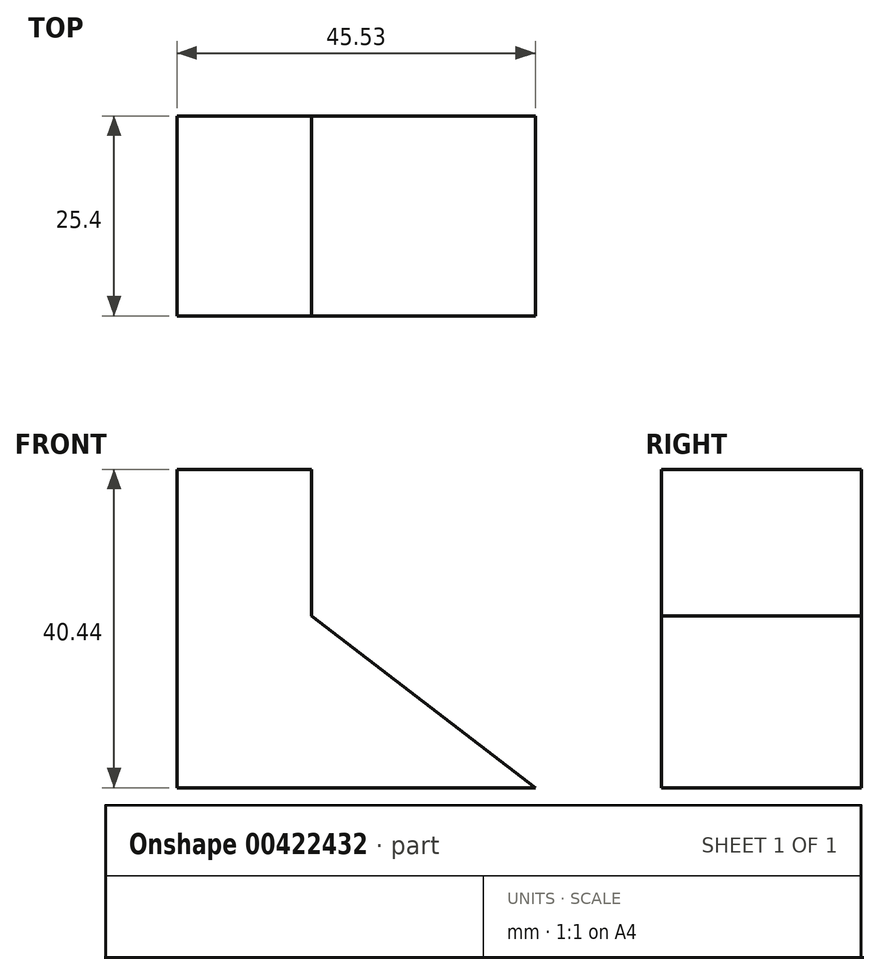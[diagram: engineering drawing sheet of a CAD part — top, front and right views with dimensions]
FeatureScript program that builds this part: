
annotation { "Feature Type Name" : "Feature", "Feature Type Description" : "" }
export const myFeature = defineFeature(function(context is Context, id is Id, definition is map)
    precondition{}
    {
        {
            var Q0;
            Q0=qCreatedBy(makeId("Front.planeOp"),FACE);
            var sketch = newSketch(context, id + "F0", { "sketchPlane" : qUnion([Q0])});
            skLineSegment(sketch, "E0", {"start": v(0, 0) * mm, "end": v(0, 40.44) * mm});
            skLineSegment(sketch, "E1", {"start": v(0, 40.44) * mm, "end": v(17.1, 40.44) * mm});
            skLineSegment(sketch, "E2", {"start": v(17.1, 40.44) * mm, "end": v(17.1, 21.8) * mm});
            skLineSegment(sketch, "E3", {"start": v(17.1, 21.8) * mm, "end": v(45.53, 0) * mm});
            skLineSegment(sketch, "E4", {"start": v(45.53, 0) * mm, "end": v(0, 0) * mm});
            skSolve(sketch);
        }
        {
            var Q0;
            Q0=makeQuery(id+"F0.imprint","IMPRINT",FACE,{"disambiguationData":[TD([[makeQuery(id+"F0.imprint","IMPRINT",EDGE,{"derivedFrom":sQuery(id+"F0.wireOp",EDGE,"E0")}),-1.0]])]});
            extrude(context, id + "F1", {"entities" : qUnion([Q0]), "depth" : 25.4 * mm});
        }
    });
